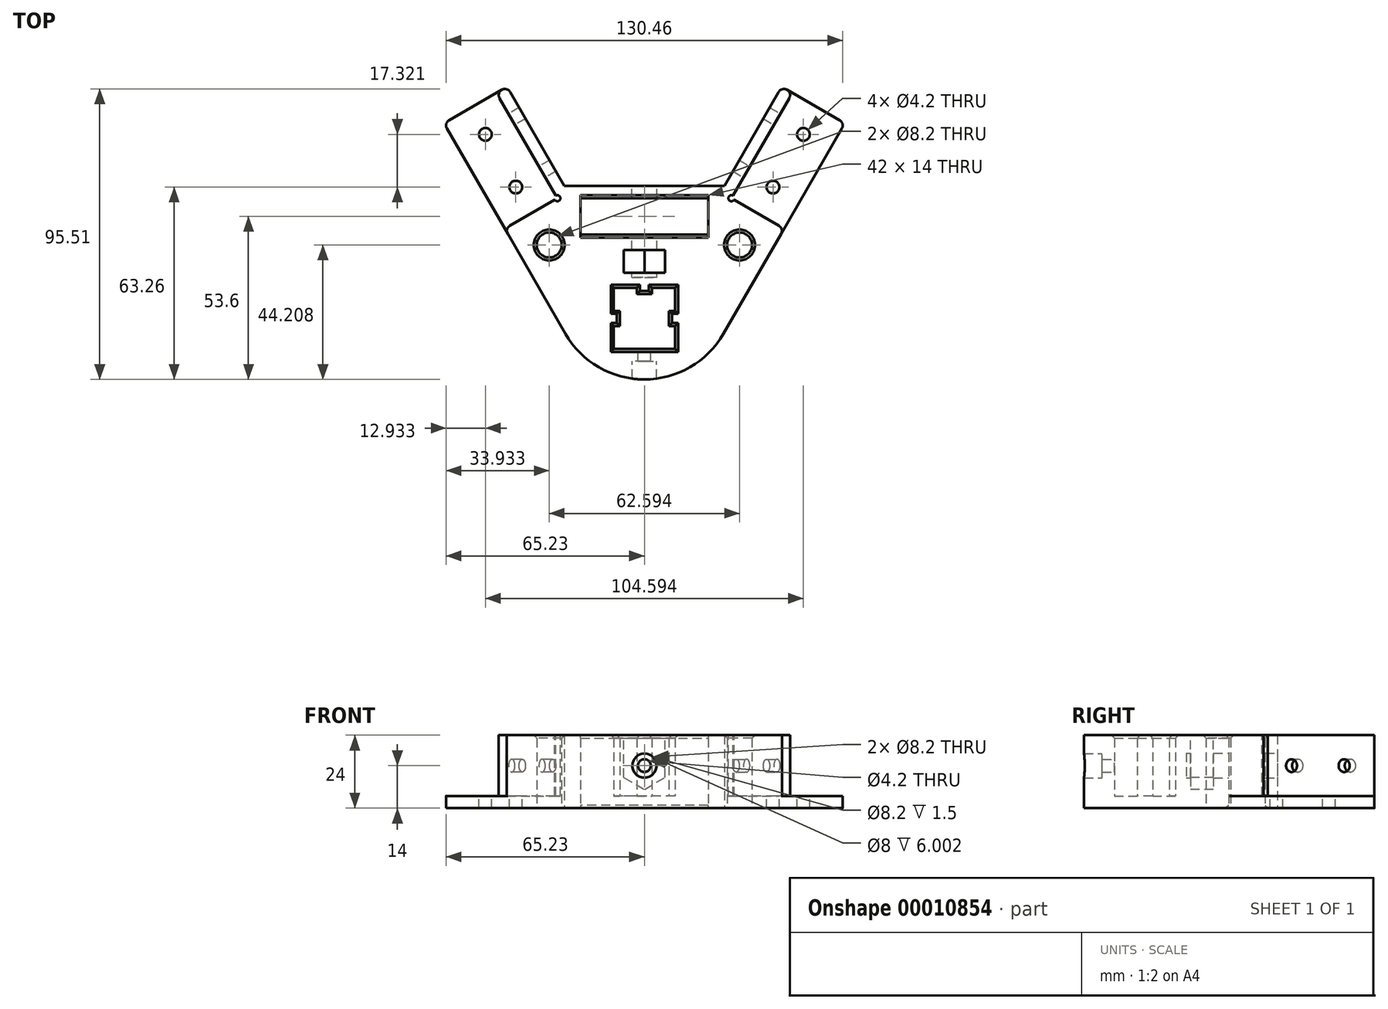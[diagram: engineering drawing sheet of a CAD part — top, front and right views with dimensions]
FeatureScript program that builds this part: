
annotation { "Feature Type Name" : "Feature", "Feature Type Description" : "" }
export const myFeature = defineFeature(function(context is Context, id is Id, definition is map)
    precondition{}
    {
        {
            var Q0;
            Q0=qCreatedBy(makeId("Top.planeOp"),FACE);
            var sketch = newSketch(context, id + "F0", { "sketchPlane" : qUnion([Q0])});
            skLineSegment(sketch, "E0.rect.bottom", {"start": v(10.05, -10.05) * mm, "end": v(-10.05, -10.05) * mm});
            skLineSegment(sketch, "E0.rect.top", {"start": v(10.05, 10.05) * mm, "end": v(-10.05, 10.05) * mm});
            skLineSegment(sketch, "E0.rect.left", {"start": v(10.05, -10.05) * mm, "end": v(10.05, 10.05) * mm});
            skLineSegment(sketch, "E0.rect.right", {"start": v(-10.05, -10.05) * mm, "end": v(-10.05, 10.05) * mm});
            skPoint(sketch, "E0.rect.middle", {"position": v(0, 0) * mm});
            skLineSegment(sketch, "E1", {"start": v(-10.05, -2.5) * mm, "end": v(-8.05, -2.5) * mm});
            skLineSegment(sketch, "E2", {"start": v(-8.05, -2.5) * mm, "end": v(-8.05, 2.5) * mm});
            skLineSegment(sketch, "E3", {"start": v(-8.05, 2.5) * mm, "end": v(-10.05, 2.5) * mm});
            skLineSegment(sketch, "E4", {"start": v(-2.5, 10.05) * mm, "end": v(-2.5, 8.05) * mm});
            skLineSegment(sketch, "E5", {"start": v(-2.5, 8.05) * mm, "end": v(2.5, 8.05) * mm});
            skLineSegment(sketch, "E6", {"start": v(2.5, 8.05) * mm, "end": v(2.5, 10.05) * mm});
            skLineSegment(sketch, "E7", {"start": v(10.05, 2.5) * mm, "end": v(8.05, 2.5) * mm});
            skLineSegment(sketch, "E8", {"start": v(8.05, 2.5) * mm, "end": v(8.05, -2.5) * mm});
            skLineSegment(sketch, "E9", {"start": v(8.05, -2.5) * mm, "end": v(10.05, -2.5) * mm});
            skLineSegment(sketch, "E10", {"start": v(-25.98, -5.05) * mm, "end": v(-65.96, 64.2) * mm});
            skLineSegment(sketch, "E11", {"start": v(-65.96, 64.2) * mm, "end": v(-45.17, 76.2) * mm});
            skLineSegment(sketch, "E12", {"start": v(-45.17, 76.2) * mm, "end": v(-25.17, 41.55) * mm});
            skLineSegment(sketch, "E13", {"start": v(-25.17, 41.55) * mm, "end": v(25.17, 41.55) * mm});
            skLineSegment(sketch, "E14", {"start": v(25.17, 41.55) * mm, "end": v(45.17, 76.2) * mm});
            skLineSegment(sketch, "E15", {"start": v(45.17, 76.2) * mm, "end": v(65.96, 64.2) * mm});
            skLineSegment(sketch, "E16", {"start": v(65.96, 64.2) * mm, "end": v(25.98, -5.05) * mm});
            skPoint(sketch, "E17.visualSharp", {"position": v(0, -50.05) * mm});
            skArc(sketch, "E17.filletArc", {"start": v(-25.98, -5.05) * mm, "mid": v(0, -20.05) * mm, "end": v(25.98, -5.05) * mm});
            skLineSegment(sketch, "E18", {"start": v(-48.64, 74.2) * mm, "end": v(-28.64, 39.55) * mm});
            skLineSegment(sketch, "E19", {"start": v(-28.64, 39.55) * mm, "end": v(-45.96, 29.55) * mm});
            skLineSegment(sketch, "E20", {"start": v(48.64, 74.2) * mm, "end": v(28.64, 39.55) * mm});
            skLineSegment(sketch, "E21", {"start": v(28.64, 39.55) * mm, "end": v(45.96, 29.55) * mm});
            skLineSegment(sketch, "E22", {"start": v(-28.64, 39.55) * mm, "end": v(-25.17, 41.55) * mm, "construction": true});
            skLineSegment(sketch, "E23", {"start": v(-57.3, 69.2) * mm, "end": v(-37.3, 34.55) * mm, "construction": true});
            skCircle(sketch, "E24", {"center": v(-52.3, 60.53) * mm, "radius": 2.1 * mm});
            skCircle(sketch, "E25", {"center": v(-42.3, 43.21) * mm, "radius": 2.1 * mm});
            skCircle(sketch, "E26", {"center": v(52.3, 60.53) * mm, "radius": 2.1 * mm});
            skCircle(sketch, "E27", {"center": v(42.3, 43.21) * mm, "radius": 2.1 * mm});
            skLineSegment(sketch, "E28", {"start": v(-21, 39.55) * mm, "end": v(21, 39.55) * mm});
            skLineSegment(sketch, "E29", {"start": v(21, 39.55) * mm, "end": v(21, 27.55) * mm});
            skLineSegment(sketch, "E30", {"start": v(10.05, 15.05) * mm, "end": v(-10.05, 15.05) * mm});
            skLineSegment(sketch, "E31", {"start": v(-21, 27.55) * mm, "end": v(-21, 39.55) * mm});
            skLineSegment(sketch, "E32", {"start": v(-21, 27.55) * mm, "end": v(-18.6, 17.84) * mm});
            skLineSegment(sketch, "E33", {"start": v(-18.6, 17.84) * mm, "end": v(-10.05, 15.05) * mm});
            skLineSegment(sketch, "E34", {"start": v(21, 27.55) * mm, "end": v(18.6, 17.84) * mm});
            skLineSegment(sketch, "E35", {"start": v(18.6, 17.84) * mm, "end": v(10.05, 15.05) * mm});
            skLineSegment(sketch, "E36", {"start": v(-37.3, 34.55) * mm, "end": v(-20.27, 5.06) * mm, "construction": true});
            skCircle(sketch, "E37", {"center": v(-31.3, 24.16) * mm, "radius": 4.1 * mm});
            skLineSegment(sketch, "E38", {"start": v(0, -71.13) * mm, "end": v(0, 233.1) * mm, "construction": true});
            skCircle(sketch, "E39", {"center": v(31.3, 24.16) * mm, "radius": 4.1 * mm});
            skLineSegment(sketch, "E40", {"start": v(-26.33, 43.55) * mm, "end": v(26.33, 43.55) * mm});
            skLineSegment(sketch, "E41", {"start": v(-21, 27.55) * mm, "end": v(21, 27.55) * mm});
            skLineSegment(sketch, "E42", {"start": v(-19.77, 22.55) * mm, "end": v(19.77, 22.55) * mm});
            skSolve(sketch);
        }
        {
            var Q0;
            {var subQ2=sQuery(id+"F0.wireOp",EDGE,"E13");Q0=makeQuery(id+"F0.imprint","IMPRINT",FACE,{"disambiguationData":[TD([[makeQuery(id+"F0.imprint","IMPRINT",EDGE,{"derivedFrom":subQ2}),1.0]])]});}
            var Q1;
            {var subQ16=sQuery(id+"F0.wireOp",EDGE,"E0.rect.bottom");Q1=makeQuery(id+"F0.imprint","IMPRINT",FACE,{"disambiguationData":[TD([[makeQuery(id+"F0.imprint","IMPRINT",EDGE,{"derivedFrom":subQ16}),1.0]])]});}
            var Q2;
            {var subQ1=sQuery(id+"F0.wireOp",EDGE,"E1");Q2=makeQuery(id+"F0.imprint","IMPRINT",FACE,{"disambiguationData":[TD([[makeQuery(id+"F0.imprint","IMPRINT",EDGE,{"derivedFrom":subQ1}),1.0]])]});}
            var Q3;
            {var subQ1=sQuery(id+"F0.wireOp",EDGE,"E4");Q3=makeQuery(id+"F0.imprint","IMPRINT",FACE,{"disambiguationData":[TD([[makeQuery(id+"F0.imprint","IMPRINT",EDGE,{"derivedFrom":subQ1}),1.0]])]});}
            var Q4;
            {var subQ1=sQuery(id+"F0.wireOp",EDGE,"E7");Q4=makeQuery(id+"F0.imprint","IMPRINT",FACE,{"disambiguationData":[TD([[makeQuery(id+"F0.imprint","IMPRINT",EDGE,{"derivedFrom":subQ1}),1.0]])]});}
            var Q5;
            {var subQ1=sQuery(id+"F0.wireOp",EDGE,"E41");Q5=makeQuery(id+"F0.imprint","IMPRINT",FACE,{"disambiguationData":[TD([[makeQuery(id+"F0.imprint","IMPRINT",EDGE,{"derivedFrom":subQ1}),-1.0]])]});}
            var Q6;
            Q6=makeQuery(id+"F0.imprint","IMPRINT",FACE,{"disambiguationData":[TD([[makeQuery(id+"F0.imprint","IMPRINT",EDGE,{"derivedFrom":sQuery(id+"F0.wireOp",EDGE,"E30")}),-1.0]])]});
            extrude(context, id + "F1", {"entities" : qUnion([Q0, Q1, Q2, Q3, Q4, Q5, Q6]), "depth" : 20 * mm});
        }
        {
            var Q0;
            {var subQ0=sQuery(id+"F0.wireOp",EDGE,"E20");Q0=makeQuery(id+"F0.imprint","IMPRINT",FACE,{"disambiguationData":[TD([[makeQuery(id+"F0.imprint","IMPRINT",EDGE,{"derivedFrom":subQ0}),1.0]])]});}
            var Q1;
            {var subQ16=sQuery(id+"F0.wireOp",EDGE,"E0.rect.bottom");Q1=makeQuery(id+"F0.imprint","IMPRINT",FACE,{"disambiguationData":[TD([[makeQuery(id+"F0.imprint","IMPRINT",EDGE,{"derivedFrom":subQ16}),1.0]])]});}
            var Q2;
            {var subQ11=sQuery(id+"F0.wireOp",EDGE,"E0.rect.bottom");Q2=makeQuery(id+"F0.imprint","IMPRINT",FACE,{"disambiguationData":[TD([[makeQuery(id+"F0.imprint","IMPRINT",EDGE,{"derivedFrom":subQ11}),-1.0]])]});}
            var Q3;
            {var subQ1=sQuery(id+"F0.wireOp",EDGE,"E18");Q3=makeQuery(id+"F0.imprint","IMPRINT",FACE,{"disambiguationData":[TD([[makeQuery(id+"F0.imprint","IMPRINT",EDGE,{"derivedFrom":subQ1}),-1.0]])]});}
            var Q4;
            {var subQ1=sQuery(id+"F0.wireOp",EDGE,"E4");Q4=makeQuery(id+"F0.imprint","IMPRINT",FACE,{"disambiguationData":[TD([[makeQuery(id+"F0.imprint","IMPRINT",EDGE,{"derivedFrom":subQ1}),1.0]])]});}
            var Q5;
            {var subQ1=sQuery(id+"F0.wireOp",EDGE,"E7");Q5=makeQuery(id+"F0.imprint","IMPRINT",FACE,{"disambiguationData":[TD([[makeQuery(id+"F0.imprint","IMPRINT",EDGE,{"derivedFrom":subQ1}),1.0]])]});}
            var Q6;
            {var subQ1=sQuery(id+"F0.wireOp",EDGE,"E1");Q6=makeQuery(id+"F0.imprint","IMPRINT",FACE,{"disambiguationData":[TD([[makeQuery(id+"F0.imprint","IMPRINT",EDGE,{"derivedFrom":subQ1}),1.0]])]});}
            var Q7;
            {var subQ2=sQuery(id+"F0.wireOp",EDGE,"E13");Q7=makeQuery(id+"F0.imprint","IMPRINT",FACE,{"disambiguationData":[TD([[makeQuery(id+"F0.imprint","IMPRINT",EDGE,{"derivedFrom":subQ2}),1.0]])]});}
            var Q8;
            {var subQ1=sQuery(id+"F0.wireOp",EDGE,"E41");Q8=makeQuery(id+"F0.imprint","IMPRINT",FACE,{"disambiguationData":[TD([[makeQuery(id+"F0.imprint","IMPRINT",EDGE,{"derivedFrom":subQ1}),-1.0]])]});}
            var Q9;
            Q9=makeQuery(id+"F0.imprint","IMPRINT",FACE,{"disambiguationData":[TD([[makeQuery(id+"F0.imprint","IMPRINT",EDGE,{"derivedFrom":sQuery(id+"F0.wireOp",EDGE,"E30")}),-1.0]])]});
            extrude(context, id + "F2", {"entities" : qUnion([Q0, Q1, Q2, Q3, Q4, Q5, Q6, Q7, Q8, Q9]), "operationType" : NewBodyOperationType.ADD, "oppositeDirection" : true, "depth" : 4 * mm});
        }
        {
            var Q0;
            {var subQ0=sQuery(id+"F0.wireOp",EDGE,"E40");Q0=makeQuery(id+"F2.boolean.opBoolean","MERGE",FACE,{"derivedFrom":[makeQuery(id+"F1.opExtrude","SWEPT_FACE",FACE,{"disambiguationData":[OSD([subQ0])]}),makeQuery(id+"F2.opExtrude","SWEPT_FACE",FACE,{"disambiguationData":[OSD([subQ0])]})]});}
            var sketch = newSketch(context, id + "F3", { "sketchPlane" : qUnion([Q0])});
            skCircle(sketch, "E43", {"center": v(0, 10) * mm, "radius": 4.1 * mm});
            skSolve(sketch);
        }
        {
            var Q0;
            Q0=makeQuery(id+"F3.imprint","IMPRINT",FACE,{"disambiguationData":[TD([[makeQuery(id+"F3.imprint","IMPRINT",EDGE,{"derivedFrom":sQuery(id+"F3.wireOp",EDGE,"E43")}),1.0]])]});
            extrude(context, id + "F4", {"entities" : qUnion([Q0]), "operationType" : NewBodyOperationType.REMOVE, "oppositeDirection" : true, "depth" : 30 * mm});
        }
        {
            var Q0;
            Q0=makeQuery(id+"F1.opExtrude","SWEPT_FACE",FACE,{"disambiguationData":[OSD([sQuery(id+"F0.wireOp",EDGE,"E20")])]});
            var sketch = newSketch(context, id + "F5", { "sketchPlane" : qUnion([Q0])});
            skCircle(sketch, "E44", {"center": v(58.57, 10) * mm, "radius": 2.1 * mm});
            skCircle(sketch, "E45", {"center": v(78.57, 10) * mm, "radius": 2.1 * mm});
            skSolve(sketch);
        }
        {
            var Q0;
            Q0 = qSketchRegion(id + "F5", true);
            extrude(context, id + "F6", {"entities" : qUnion([Q0]), "operationType" : NewBodyOperationType.REMOVE, "oppositeDirection" : true, "depth" : 25 * mm});
        }
        {
            var Q0;
            Q0=makeQuery(id+"F1.opExtrude","SWEPT_FACE",FACE,{"disambiguationData":[OSD([sQuery(id+"F0.wireOp",EDGE,"E18")])]});
            var sketch = newSketch(context, id + "F7", { "sketchPlane" : qUnion([Q0])});
            skCircle(sketch, "E46", {"center": v(-78.57, 10) * mm, "radius": 2.1 * mm});
            skCircle(sketch, "E47", {"center": v(-58.57, 10) * mm, "radius": 2.1 * mm});
            skSolve(sketch);
        }
        {
            var Q0;
            Q0 = qSketchRegion(id + "F7", true);
            extrude(context, id + "F8", {"entities" : qUnion([Q0]), "operationType" : NewBodyOperationType.REMOVE, "oppositeDirection" : true, "depth" : 25 * mm});
        }
        {
            var Q0;
            Q0=makeQuery(id+"F1.opExtrude","CAP_FACE",FACE,{"disambiguationData":[OSD([sQuery(id+"F0.wireOp",EDGE,"E0.rect.bottom"),sQuery(id+"F0.wireOp",EDGE,"E0.rect.top"),sQuery(id+"F0.wireOp",EDGE,"E0.rect.left"),sQuery(id+"F0.wireOp",EDGE,"E0.rect.right"),sQuery(id+"F0.wireOp",EDGE,"E1"),sQuery(id+"F0.wireOp",EDGE,"E2"),sQuery(id+"F0.wireOp",EDGE,"E3"),sQuery(id+"F0.wireOp",EDGE,"E4"),sQuery(id+"F0.wireOp",EDGE,"E5"),sQuery(id+"F0.wireOp",EDGE,"E6"),sQuery(id+"F0.wireOp",EDGE,"E7"),sQuery(id+"F0.wireOp",EDGE,"E8"),sQuery(id+"F0.wireOp",EDGE,"E9"),sQuery(id+"F0.wireOp",EDGE,"E10"),sQuery(id+"F0.wireOp",EDGE,"E11"),sQuery(id+"F0.wireOp",EDGE,"E12"),sQuery(id+"F0.wireOp",EDGE,"E14"),sQuery(id+"F0.wireOp",EDGE,"E15"),sQuery(id+"F0.wireOp",EDGE,"E16"),sQuery(id+"F0.wireOp",EDGE,"E17.filletArc"),sQuery(id+"F0.wireOp",EDGE,"E18"),sQuery(id+"F0.wireOp",EDGE,"E19"),sQuery(id+"F0.wireOp",EDGE,"E20"),sQuery(id+"F0.wireOp",EDGE,"E21"),sQuery(id+"F0.wireOp",EDGE,"E28"),sQuery(id+"F0.wireOp",EDGE,"E29"),sQuery(id+"F0.wireOp",EDGE,"E31"),sQuery(id+"F0.wireOp",EDGE,"E37"),sQuery(id+"F0.wireOp",EDGE,"E39"),sQuery(id+"F0.wireOp",EDGE,"E40"),sQuery(id+"F0.wireOp",EDGE,"E41")])],"isStart":false});
            var sketch = newSketch(context, id + "F9", { "sketchPlane" : qUnion([Q0])});
            skLineSegment(sketch, "E48.rect.bottom", {"start": v(6.75, 15.05) * mm, "end": v(-6.75, 15.05) * mm});
            skLineSegment(sketch, "E48.rect.top", {"start": v(6.75, 22.55) * mm, "end": v(-6.75, 22.55) * mm});
            skLineSegment(sketch, "E48.rect.left", {"start": v(6.75, 15.05) * mm, "end": v(6.75, 22.55) * mm});
            skLineSegment(sketch, "E48.rect.right", {"start": v(-6.75, 15.05) * mm, "end": v(-6.75, 22.55) * mm});
            skPoint(sketch, "E48.rect.middle", {"position": v(0, 18.8) * mm});
            skSolve(sketch);
        }
        {
            var Q0;
            Q0=makeQuery(id+"F9.imprint","IMPRINT",FACE,{"disambiguationData":[TD([[makeQuery(id+"F9.imprint","IMPRINT",EDGE,{"derivedFrom":sQuery(id+"F9.wireOp",EDGE,"E48.rect.bottom")}),-1.0]])]});
            extrude(context, id + "F10", {"entities" : qUnion([Q0]), "operationType" : NewBodyOperationType.REMOVE, "oppositeDirection" : true, "depth" : 10 * mm});
        }
        {
            var Q0;
            Q0=makeQuery(id+"F10.boolean.opBoolean","COPY",FACE,{"derivedFrom":makeQuery(id+"F10.opExtrude","SWEPT_FACE",FACE,{"disambiguationData":[OSD([sQuery(id+"F9.wireOp",EDGE,"E48.rect.bottom")])]})});
            var sketch = newSketch(context, id + "F11", { "sketchPlane" : qUnion([Q0])});
            skCircle(sketch, "E49.cCircle", {"center": v(0, 10) * mm, "radius": 6.75 * mm, "construction": true});
            skLineSegment(sketch, "E49.0", {"start": v(6.75, 6.1) * mm, "end": v(0, 2.2) * mm});
            skLineSegment(sketch, "E49.1", {"start": v(0, 2.2) * mm, "end": v(-6.75, 6.1) * mm});
            skLineSegment(sketch, "E49.2", {"start": v(-6.75, 6.1) * mm, "end": v(-6.75, 13.9) * mm});
            skLineSegment(sketch, "E49.3", {"start": v(-6.75, 13.9) * mm, "end": v(0, 17.8) * mm});
            skLineSegment(sketch, "E49.4", {"start": v(0, 17.8) * mm, "end": v(6.75, 13.9) * mm});
            skLineSegment(sketch, "E49.5", {"start": v(6.75, 13.9) * mm, "end": v(6.75, 6.1) * mm});
            skPoint(sketch, "E49.0.midPoint", {"position": v(3.37, 4.15) * mm});
            skSolve(sketch);
        }
        {
            var Q0;
            Q0 = qSketchRegion(id + "F11", true);
            var Q1;
            Q1=makeQuery(id+"F10.boolean.opBoolean","COPY",FACE,{"derivedFrom":makeQuery(id+"F10.opExtrude","SWEPT_FACE",FACE,{"disambiguationData":[OSD([sQuery(id+"F9.wireOp",EDGE,"E48.rect.top")])]})});
            extrude(context, id + "F12", {"entities" : qUnion([Q0]), "operationType" : NewBodyOperationType.REMOVE, "endBound" : BoundingType.UP_TO_SURFACE, "endBoundEntityFace" : qUnion([Q1]), "depth" : 25 * mm});
        }
        {
            var Q0;
            Q0=makeQuery(id+"F1.opExtrude","CAP_FACE",FACE,{"disambiguationData":[OSD([sQuery(id+"F0.wireOp",EDGE,"E0.rect.bottom"),sQuery(id+"F0.wireOp",EDGE,"E0.rect.top"),sQuery(id+"F0.wireOp",EDGE,"E0.rect.left"),sQuery(id+"F0.wireOp",EDGE,"E0.rect.right"),sQuery(id+"F0.wireOp",EDGE,"E1"),sQuery(id+"F0.wireOp",EDGE,"E2"),sQuery(id+"F0.wireOp",EDGE,"E3"),sQuery(id+"F0.wireOp",EDGE,"E4"),sQuery(id+"F0.wireOp",EDGE,"E5"),sQuery(id+"F0.wireOp",EDGE,"E6"),sQuery(id+"F0.wireOp",EDGE,"E7"),sQuery(id+"F0.wireOp",EDGE,"E8"),sQuery(id+"F0.wireOp",EDGE,"E9"),sQuery(id+"F0.wireOp",EDGE,"E10"),sQuery(id+"F0.wireOp",EDGE,"E11"),sQuery(id+"F0.wireOp",EDGE,"E12"),sQuery(id+"F0.wireOp",EDGE,"E14"),sQuery(id+"F0.wireOp",EDGE,"E15"),sQuery(id+"F0.wireOp",EDGE,"E16"),sQuery(id+"F0.wireOp",EDGE,"E17.filletArc"),sQuery(id+"F0.wireOp",EDGE,"E18"),sQuery(id+"F0.wireOp",EDGE,"E19"),sQuery(id+"F0.wireOp",EDGE,"E20"),sQuery(id+"F0.wireOp",EDGE,"E21"),sQuery(id+"F0.wireOp",EDGE,"E28"),sQuery(id+"F0.wireOp",EDGE,"E29"),sQuery(id+"F0.wireOp",EDGE,"E31"),sQuery(id+"F0.wireOp",EDGE,"E37"),sQuery(id+"F0.wireOp",EDGE,"E39"),sQuery(id+"F0.wireOp",EDGE,"E40"),sQuery(id+"F0.wireOp",EDGE,"E41")])],"isStart":false});
            var sketch = newSketch(context, id + "F13", { "sketchPlane" : qUnion([Q0])});
            skCircle(sketch, "E50", {"center": v(28.64, 39.55) * mm, "radius": 1 * mm});
            skCircle(sketch, "E51", {"center": v(-28.64, 39.55) * mm, "radius": 1 * mm});
            skSolve(sketch);
        }
        {
            var Q0;
            {var subQ1=sQuery(id+"F13.wireOp",EDGE,"E50");var subQ3=makeQuery(id+"F1.opExtrude","CAP_EDGE",EDGE,{"disambiguationData":[OSD([sQuery(id+"F0.wireOp",EDGE,"E20")])],"isStart":false});var subQ5=makeQuery(id+"F13.imprint","INTERSECT",VERTEX,{"derivedFrom":[subQ3,subQ1]});Q0=makeQuery(id+"F13.imprint","IMPRINT",FACE,{"disambiguationData":[TD([[makeQuery(id+"F13.imprint","IMPRINT",EDGE,{"disambiguationData":[TD([[subQ5,-1.0]])],"derivedFrom":subQ1}),1.0]])]});}
            var Q1;
            {var subQ1=sQuery(id+"F13.wireOp",EDGE,"E51");var subQ3=makeQuery(id+"F1.opExtrude","CAP_EDGE",EDGE,{"disambiguationData":[OSD([sQuery(id+"F0.wireOp",EDGE,"E18")])],"isStart":false});var subQ5=makeQuery(id+"F13.imprint","INTERSECT",VERTEX,{"derivedFrom":[subQ3,subQ1]});Q1=makeQuery(id+"F13.imprint","IMPRINT",FACE,{"disambiguationData":[TD([[makeQuery(id+"F13.imprint","IMPRINT",EDGE,{"disambiguationData":[TD([[subQ5,1.0]])],"derivedFrom":subQ1}),1.0]])]});}
            var Q2;
            {var subQ0=sQuery(id+"F0.wireOp",EDGE,"E15");var subQ1=sQuery(id+"F0.wireOp",EDGE,"E16");var subQ2=sQuery(id+"F0.wireOp",EDGE,"E26");var subQ3=sQuery(id+"F0.wireOp",EDGE,"E27");Q2=makeQuery(id+"F2.boolean.opBoolean","SPLIT",FACE,{"disambiguationData":[TD([makeQuery(id+"F1.opExtrude","SWEPT_FACE",FACE,{"disambiguationData":[OSD([subQ0])]})])],"derivedFrom":makeQuery(id+"F2.opExtrude","CAP_FACE",FACE,{"disambiguationData":[OSD([sQuery(id+"F0.wireOp",EDGE,"E10"),sQuery(id+"F0.wireOp",EDGE,"E11"),sQuery(id+"F0.wireOp",EDGE,"E12"),sQuery(id+"F0.wireOp",EDGE,"E14"),subQ0,subQ1,sQuery(id+"F0.wireOp",EDGE,"E17.filletArc"),sQuery(id+"F0.wireOp",EDGE,"E24"),sQuery(id+"F0.wireOp",EDGE,"E25"),subQ2,subQ3,sQuery(id+"F0.wireOp",EDGE,"E28"),sQuery(id+"F0.wireOp",EDGE,"E29"),sQuery(id+"F0.wireOp",EDGE,"E31"),sQuery(id+"F0.wireOp",EDGE,"E40"),sQuery(id+"F0.wireOp",EDGE,"E41")])],"isStart":true})});}
            extrude(context, id + "F14", {"entities" : qUnion([Q0, Q1]), "operationType" : NewBodyOperationType.REMOVE, "endBound" : BoundingType.UP_TO_SURFACE, "oppositeDirection" : true, "endBoundEntityFace" : qUnion([Q2]), "depth" : 25 * mm});
        }
        {
            var Q0;
            Q0=makeQuery(id+"F1.opExtrude","SWEPT_EDGE",EDGE,{"disambiguationData":[OSD([sQuery(id+"F0.wireOp",EDGE,"E11"),sQuery(id+"F0.wireOp",EDGE,"E18")])]});
            var Q1;
            {var subQ0=sQuery(id+"F0.wireOp",EDGE,"E11");var subQ1=sQuery(id+"F0.wireOp",EDGE,"E12");Q1=makeQuery(id+"F2.boolean.opBoolean","MERGE",EDGE,{"derivedFrom":[makeQuery(id+"F1.opExtrude","SWEPT_EDGE",EDGE,{"disambiguationData":[OSD([subQ0,subQ1])]}),makeQuery(id+"F2.opExtrude","SWEPT_EDGE",EDGE,{"disambiguationData":[OSD([subQ0,subQ1])]})]});}
            var Q2;
            Q2=makeQuery(id+"F1.opExtrude","SWEPT_EDGE",EDGE,{"disambiguationData":[OSD([sQuery(id+"F0.wireOp",EDGE,"E10"),sQuery(id+"F0.wireOp",EDGE,"E19")])]});
            var Q3;
            Q3=makeQuery(id+"F14.boolean.opBoolean","COPY",EDGE,{"derivedFrom":makeQuery(id+"F14.opExtrude","SWEPT_EDGE",EDGE,{"disambiguationData":[OSD([sQuery(id+"F0.wireOp",EDGE,"E19"),sQuery(id+"F13.wireOp",EDGE,"E51")])]})});
            var Q4;
            Q4=makeQuery(id+"F14.boolean.opBoolean","COPY",EDGE,{"derivedFrom":makeQuery(id+"F14.opExtrude","SWEPT_EDGE",EDGE,{"disambiguationData":[OSD([sQuery(id+"F0.wireOp",EDGE,"E18"),sQuery(id+"F13.wireOp",EDGE,"E51")])]})});
            var Q5;
            Q5=makeQuery(id+"F2.opExtrude","SWEPT_EDGE",EDGE,{"disambiguationData":[OSD([sQuery(id+"F0.wireOp",EDGE,"E10"),sQuery(id+"F0.wireOp",EDGE,"E11")])]});
            var Q6;
            {var subQ0=sQuery(id+"F0.wireOp",EDGE,"E14");var subQ1=sQuery(id+"F0.wireOp",EDGE,"E15");Q6=makeQuery(id+"F2.boolean.opBoolean","MERGE",EDGE,{"derivedFrom":[makeQuery(id+"F1.opExtrude","SWEPT_EDGE",EDGE,{"disambiguationData":[OSD([subQ0,subQ1])]}),makeQuery(id+"F2.opExtrude","SWEPT_EDGE",EDGE,{"disambiguationData":[OSD([subQ0,subQ1])]})]});}
            var Q7;
            Q7=makeQuery(id+"F1.opExtrude","SWEPT_EDGE",EDGE,{"disambiguationData":[OSD([sQuery(id+"F0.wireOp",EDGE,"E15"),sQuery(id+"F0.wireOp",EDGE,"E20")])]});
            var Q8;
            Q8=makeQuery(id+"F2.opExtrude","SWEPT_EDGE",EDGE,{"disambiguationData":[OSD([sQuery(id+"F0.wireOp",EDGE,"E15"),sQuery(id+"F0.wireOp",EDGE,"E16")])]});
            var Q9;
            Q9=makeQuery(id+"F1.opExtrude","SWEPT_EDGE",EDGE,{"disambiguationData":[OSD([sQuery(id+"F0.wireOp",EDGE,"E16"),sQuery(id+"F0.wireOp",EDGE,"E21")])]});
            var Q10;
            Q10=makeQuery(id+"F14.boolean.opBoolean","COPY",EDGE,{"derivedFrom":makeQuery(id+"F14.opExtrude","SWEPT_EDGE",EDGE,{"disambiguationData":[OSD([sQuery(id+"F0.wireOp",EDGE,"E21"),sQuery(id+"F13.wireOp",EDGE,"E50")])]})});
            var Q11;
            Q11=makeQuery(id+"F14.boolean.opBoolean","COPY",EDGE,{"derivedFrom":makeQuery(id+"F14.opExtrude","SWEPT_EDGE",EDGE,{"disambiguationData":[OSD([sQuery(id+"F0.wireOp",EDGE,"E20"),sQuery(id+"F13.wireOp",EDGE,"E50")])]})});
            fillet(context, id + "F15", {"entities" : qUnion([Q0, Q1, Q2, Q3, Q4, Q5, Q6, Q7, Q8, Q9, Q10, Q11]), "radius" : 2 * mm, "tangentPropagation" : true, "allowEdgeOverflow" : false});
        }
        {
            var Q0;
            Q0=makeQuery(id+"F10.boolean.opBoolean","COPY",EDGE,{"derivedFrom":makeQuery(id+"F10.opExtrude","CAP_EDGE",EDGE,{"disambiguationData":[OSD([sQuery(id+"F9.wireOp",EDGE,"E48.rect.top")])],"isStart":true})});
            var Q1;
            Q1=makeQuery(id+"F10.boolean.opBoolean","COPY",EDGE,{"derivedFrom":makeQuery(id+"F10.opExtrude","CAP_EDGE",EDGE,{"disambiguationData":[OSD([sQuery(id+"F9.wireOp",EDGE,"E48.rect.left")])],"isStart":true})});
            var Q2;
            Q2=makeQuery(id+"F10.boolean.opBoolean","COPY",EDGE,{"derivedFrom":makeQuery(id+"F10.opExtrude","CAP_EDGE",EDGE,{"disambiguationData":[OSD([sQuery(id+"F9.wireOp",EDGE,"E48.rect.bottom")])],"isStart":true})});
            var Q3;
            Q3=makeQuery(id+"F10.boolean.opBoolean","COPY",EDGE,{"derivedFrom":makeQuery(id+"F10.opExtrude","CAP_EDGE",EDGE,{"disambiguationData":[OSD([sQuery(id+"F9.wireOp",EDGE,"E48.rect.right")])],"isStart":true})});
            var Q4;
            {var subQ0=sQuery(id+"F0.wireOp",EDGE,"E0.rect.top");Q4=makeQuery(id+"F1.opExtrude","CAP_EDGE",EDGE,{"disambiguationData":[OSD([subQ0]),TDD([makeQuery(id+"F0.imprint","IMPRINT",EDGE,{"disambiguationData":[TD([[makeQuery(id+"F0.imprint","INTERSECT",VERTEX,{"derivedFrom":[subQ0,sQuery(id+"F0.wireOp",EDGE,"E0.rect.right")]}),1.0]])],"derivedFrom":subQ0})])],"isStart":false});}
            var Q5;
            Q5=makeQuery(id+"F1.opExtrude","CAP_EDGE",EDGE,{"disambiguationData":[OSD([sQuery(id+"F0.wireOp",EDGE,"E4")])],"isStart":false});
            var Q6;
            Q6=makeQuery(id+"F1.opExtrude","CAP_EDGE",EDGE,{"disambiguationData":[OSD([sQuery(id+"F0.wireOp",EDGE,"E5")])],"isStart":false});
            var Q7;
            Q7=makeQuery(id+"F1.opExtrude","CAP_EDGE",EDGE,{"disambiguationData":[OSD([sQuery(id+"F0.wireOp",EDGE,"E6")])],"isStart":false});
            var Q8;
            {var subQ0=sQuery(id+"F0.wireOp",EDGE,"E0.rect.top");Q8=makeQuery(id+"F1.opExtrude","CAP_EDGE",EDGE,{"disambiguationData":[OSD([subQ0]),TDD([makeQuery(id+"F0.imprint","IMPRINT",EDGE,{"disambiguationData":[TD([[makeQuery(id+"F0.imprint","INTERSECT",VERTEX,{"derivedFrom":[subQ0,sQuery(id+"F0.wireOp",EDGE,"E0.rect.left")]}),-1.0]])],"derivedFrom":subQ0})])],"isStart":false});}
            var Q9;
            {var subQ0=sQuery(id+"F0.wireOp",EDGE,"E0.rect.left");Q9=makeQuery(id+"F1.opExtrude","CAP_EDGE",EDGE,{"disambiguationData":[OSD([subQ0]),TDD([makeQuery(id+"F0.imprint","IMPRINT",EDGE,{"disambiguationData":[TD([[makeQuery(id+"F0.imprint","INTERSECT",VERTEX,{"derivedFrom":[sQuery(id+"F0.wireOp",EDGE,"E0.rect.top"),subQ0]}),1.0]])],"derivedFrom":subQ0})])],"isStart":false});}
            var Q10;
            Q10=makeQuery(id+"F1.opExtrude","CAP_EDGE",EDGE,{"disambiguationData":[OSD([sQuery(id+"F0.wireOp",EDGE,"E7")])],"isStart":false});
            var Q11;
            Q11=makeQuery(id+"F1.opExtrude","CAP_EDGE",EDGE,{"disambiguationData":[OSD([sQuery(id+"F0.wireOp",EDGE,"E8")])],"isStart":false});
            var Q12;
            Q12=makeQuery(id+"F1.opExtrude","CAP_EDGE",EDGE,{"disambiguationData":[OSD([sQuery(id+"F0.wireOp",EDGE,"E9")])],"isStart":false});
            var Q13;
            {var subQ0=sQuery(id+"F0.wireOp",EDGE,"E0.rect.left");Q13=makeQuery(id+"F1.opExtrude","CAP_EDGE",EDGE,{"disambiguationData":[OSD([subQ0]),TDD([makeQuery(id+"F0.imprint","IMPRINT",EDGE,{"disambiguationData":[TD([[makeQuery(id+"F0.imprint","INTERSECT",VERTEX,{"derivedFrom":[sQuery(id+"F0.wireOp",EDGE,"E0.rect.bottom"),subQ0]}),-1.0]])],"derivedFrom":subQ0})])],"isStart":false});}
            var Q14;
            Q14=makeQuery(id+"F1.opExtrude","CAP_EDGE",EDGE,{"disambiguationData":[OSD([sQuery(id+"F0.wireOp",EDGE,"E0.rect.bottom")])],"isStart":false});
            var Q15;
            {var subQ0=sQuery(id+"F0.wireOp",EDGE,"E0.rect.right");Q15=makeQuery(id+"F1.opExtrude","CAP_EDGE",EDGE,{"disambiguationData":[OSD([subQ0]),TDD([makeQuery(id+"F0.imprint","IMPRINT",EDGE,{"disambiguationData":[TD([[makeQuery(id+"F0.imprint","INTERSECT",VERTEX,{"derivedFrom":[sQuery(id+"F0.wireOp",EDGE,"E0.rect.bottom"),subQ0]}),-1.0]])],"derivedFrom":subQ0})])],"isStart":false});}
            var Q16;
            Q16=makeQuery(id+"F1.opExtrude","CAP_EDGE",EDGE,{"disambiguationData":[OSD([sQuery(id+"F0.wireOp",EDGE,"E1")])],"isStart":false});
            var Q17;
            {var subQ0=sQuery(id+"F0.wireOp",EDGE,"E0.rect.right");Q17=makeQuery(id+"F1.opExtrude","CAP_EDGE",EDGE,{"disambiguationData":[OSD([subQ0]),TDD([makeQuery(id+"F0.imprint","IMPRINT",EDGE,{"disambiguationData":[TD([[makeQuery(id+"F0.imprint","INTERSECT",VERTEX,{"derivedFrom":[sQuery(id+"F0.wireOp",EDGE,"E0.rect.top"),subQ0]}),1.0]])],"derivedFrom":subQ0})])],"isStart":false});}
            var Q18;
            Q18=makeQuery(id+"F1.opExtrude","CAP_EDGE",EDGE,{"disambiguationData":[OSD([sQuery(id+"F0.wireOp",EDGE,"E3")])],"isStart":false});
            var Q19;
            Q19=makeQuery(id+"F1.opExtrude","CAP_EDGE",EDGE,{"disambiguationData":[OSD([sQuery(id+"F0.wireOp",EDGE,"E2")])],"isStart":false});
            var Q20;
            Q20=makeQuery(id+"F1.opExtrude","CAP_EDGE",EDGE,{"disambiguationData":[OSD([sQuery(id+"F0.wireOp",EDGE,"E39")])],"isStart":false});
            var Q21;
            Q21=makeQuery(id+"F1.opExtrude","CAP_EDGE",EDGE,{"disambiguationData":[OSD([sQuery(id+"F0.wireOp",EDGE,"E37")])],"isStart":false});
            var Q22;
            Q22=makeQuery(id+"F1.opExtrude","CAP_EDGE",EDGE,{"disambiguationData":[OSD([sQuery(id+"F0.wireOp",EDGE,"E28")])],"isStart":false});
            var Q23;
            Q23=makeQuery(id+"F1.opExtrude","CAP_EDGE",EDGE,{"disambiguationData":[OSD([sQuery(id+"F0.wireOp",EDGE,"E41")])],"isStart":false});
            var Q24;
            Q24=makeQuery(id+"F2.opExtrude","CAP_EDGE",EDGE,{"disambiguationData":[OSD([sQuery(id+"F0.wireOp",EDGE,"E41")])],"isStart":false});
            var Q25;
            Q25=makeQuery(id+"F2.opExtrude","CAP_EDGE",EDGE,{"disambiguationData":[OSD([sQuery(id+"F0.wireOp",EDGE,"E28")])],"isStart":false});
            chamfer(context, id + "F16", {"entities" : qUnion([Q0, Q1, Q2, Q3, Q4, Q5, Q6, Q7, Q8, Q9, Q10, Q11, Q12, Q13, Q14, Q15, Q16, Q17, Q18, Q19, Q20, Q21, Q22, Q23, Q24, Q25]), "width" : 1 * mm, "tangentPropagation" : true});
        }
        {
            var Q0;
            Q0=qCreatedBy(makeId("Front.planeOp"),FACE);
            var sketch = newSketch(context, id + "F17", { "sketchPlane" : qUnion([Q0])});
            skCircle(sketch, "E52", {"center": v(0, 10) * mm, "radius": 2.1 * mm});
            skCircle(sketch, "E53", {"center": v(0, 10) * mm, "radius": 4 * mm});
            skSolve(sketch);
        }
        {
            var Q0;
            Q0=makeQuery(id+"F17.imprint","IMPRINT",FACE,{"disambiguationData":[TD([[makeQuery(id+"F17.imprint","IMPRINT",EDGE,{"derivedFrom":sQuery(id+"F17.wireOp",EDGE,"E52")}),1.0]])]});
            extrude(context, id + "F18", {"entities" : qUnion([Q0]), "operationType" : NewBodyOperationType.REMOVE, "endBound" : BoundingType.THROUGH_ALL, "depth" : 25 * mm});
        }
        {
            var Q0;
            Q0=makeQuery(id+"F17.imprint","IMPRINT",FACE,{"disambiguationData":[TD([[makeQuery(id+"F17.imprint","IMPRINT",EDGE,{"derivedFrom":sQuery(id+"F17.wireOp",EDGE,"E52")}),-1.0]])]});
            extrude(context, id + "F19", {"entities" : qUnion([Q0]), "operationType" : NewBodyOperationType.REMOVE, "depth" : 25 * mm, "hasSecondDirection" : true, "secondDirectionOppositeDirection" : false, "secondDirectionDepth" : 14.05 * mm});
        }
    });
